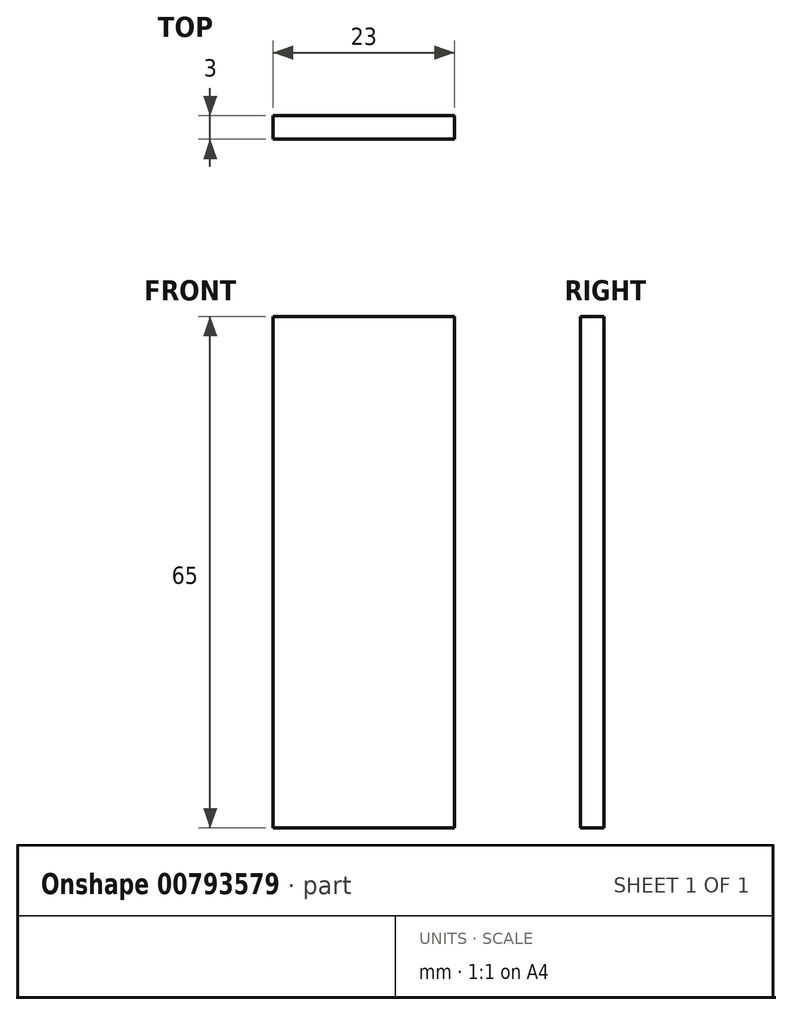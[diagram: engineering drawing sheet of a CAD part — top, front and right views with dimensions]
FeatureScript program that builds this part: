
annotation { "Feature Type Name" : "Feature", "Feature Type Description" : "" }
export const myFeature = defineFeature(function(context is Context, id is Id, definition is map)
    precondition{}
    {
        {
            var Q0;
            Q0=qCreatedBy(makeId("Front.planeOp"),FACE);
            var sketch = newSketch(context, id + "F0", { "sketchPlane" : qUnion([Q0])});
            skLineSegment(sketch, "E0.bottom", {"start": v(-60.68, 32.5) * mm, "end": v(49.32, 32.5) * mm});
            skLineSegment(sketch, "E0.top", {"start": v(-60.68, -32.5) * mm, "end": v(49.32, -32.5) * mm});
            skLineSegment(sketch, "E0.left", {"start": v(-60.68, 32.5) * mm, "end": v(-60.68, -32.5) * mm});
            skLineSegment(sketch, "E0.right", {"start": v(49.32, 32.5) * mm, "end": v(49.32, -32.5) * mm});
            skLineSegment(sketch, "E1.bottom", {"start": v(-14.35, 50) * mm, "end": v(8.65, 50) * mm});
            skLineSegment(sketch, "E1.top", {"start": v(-14.35, -50) * mm, "end": v(8.65, -50) * mm});
            skLineSegment(sketch, "E1.left", {"start": v(-14.35, 50) * mm, "end": v(-14.35, -50) * mm});
            skLineSegment(sketch, "E1.right", {"start": v(8.65, 50) * mm, "end": v(8.65, -50) * mm});
            skLineSegment(sketch, "E2", {"start": v(-14.35, 50) * mm, "end": v(-41, 32.5) * mm});
            skLineSegment(sketch, "E3", {"start": v(8.65, 50) * mm, "end": v(35.13, 32.5) * mm});
            skLineSegment(sketch, "E4", {"start": v(8.65, -50) * mm, "end": v(35.2, -32.5) * mm});
            skLineSegment(sketch, "E5", {"start": v(-14.35, -50) * mm, "end": v(-40.71, -32.5) * mm});
            skSolve(sketch);
        }
        {
            var Q0;
            Q0 = qSketchRegion(id + "F0", true);
            extrude(context, id + "F1", {"entities" : qUnion([Q0]), "depth" : 3 * mm, "offsetDistance" : 25 * mm});
        }
        {
            var Q0;
            Q0=makeQuery(id+"F1.opExtrude","CAP_FACE",FACE,{"disambiguationData":[OSD([sQuery(id+"F0.wireOp",EDGE,"E0.bottom"),sQuery(id+"F0.wireOp",EDGE,"E0.top"),sQuery(id+"F0.wireOp",EDGE,"E0.left"),sQuery(id+"F0.wireOp",EDGE,"E0.right"),sQuery(id+"F0.wireOp",EDGE,"E1.bottom"),sQuery(id+"F0.wireOp",EDGE,"E1.top"),sQuery(id+"F0.wireOp",EDGE,"E1.left"),sQuery(id+"F0.wireOp",EDGE,"E1.right"),sQuery(id+"F0.wireOp",EDGE,"E2"),sQuery(id+"F0.wireOp",EDGE,"E3"),sQuery(id+"F0.wireOp",EDGE,"E4"),sQuery(id+"F0.wireOp",EDGE,"E5")])],"isStart":false});
            var sketch = newSketch(context, id + "F2", { "sketchPlane" : qUnion([Q0])});
            skLineSegment(sketch, "E6.bottom", {"start": v(-14.35, 32.5) * mm, "end": v(8.65, 32.5) * mm});
            skLineSegment(sketch, "E6.top", {"start": v(-14.35, -32.5) * mm, "end": v(8.65, -32.5) * mm});
            skLineSegment(sketch, "E6.left", {"start": v(-14.35, 32.5) * mm, "end": v(-14.35, -32.5) * mm});
            skLineSegment(sketch, "E6.right", {"start": v(8.65, 32.5) * mm, "end": v(8.65, -32.5) * mm});
            skSolve(sketch);
        }
        {
            var Q0;
            Q0=makeQuery(id+"F2.imprint","IMPRINT",FACE,{"disambiguationData":[TD([[makeQuery(id+"F2.imprint","IMPRINT",EDGE,{"derivedFrom":sQuery(id+"F2.wireOp",EDGE,"E6.bottom")}),-1.0]])]});
            extrude(context, id + "F3", {"entities" : qUnion([Q0]), "depth" : 3 * mm, "offsetDistance" : 25 * mm});
        }
        {
            var Q0;
            Q0=makeQuery(id+"F1.opExtrude","CAP_FACE",FACE,{"disambiguationData":[OSD([sQuery(id+"F0.wireOp",EDGE,"E0.bottom"),sQuery(id+"F0.wireOp",EDGE,"E0.top"),sQuery(id+"F0.wireOp",EDGE,"E0.left"),sQuery(id+"F0.wireOp",EDGE,"E0.right"),sQuery(id+"F0.wireOp",EDGE,"E1.bottom"),sQuery(id+"F0.wireOp",EDGE,"E1.top"),sQuery(id+"F0.wireOp",EDGE,"E1.left"),sQuery(id+"F0.wireOp",EDGE,"E1.right"),sQuery(id+"F0.wireOp",EDGE,"E2"),sQuery(id+"F0.wireOp",EDGE,"E3"),sQuery(id+"F0.wireOp",EDGE,"E4"),sQuery(id+"F0.wireOp",EDGE,"E5")])],"isStart":false});
            var sketch = newSketch(context, id + "F4", { "sketchPlane" : qUnion([Q0])});
            skCircle(sketch, "E7", {"center": v(-15.85, 41.04) * mm, "radius": 1.5 * mm});
            skCircle(sketch, "E8", {"center": v(15.17, 41.61) * mm, "radius": 1.83 * mm});
            skSolve(sketch);
        }
        {
            var Q0;
            Q0=makeQuery(id+"F4.imprint","IMPRINT",FACE,{"disambiguationData":[TD([[makeQuery(id+"F4.imprint","IMPRINT",EDGE,{"derivedFrom":sQuery(id+"F4.wireOp",EDGE,"E8")}),1.0]])]});
            extrude(context, id + "F5", {"entities" : qUnion([Q0]), "operationType" : NewBodyOperationType.REMOVE, "oppositeDirection" : true, "depth" : 25 * mm, "offsetDistance" : 25 * mm});
        }
        {
            var Q0;
            Q0 = qSketchRegion(id + "F4", true);
            var Q1;
            Q1=makeQuery(id+"F1.opExtrude","CAP_FACE",FACE,{"disambiguationData":[OSD([sQuery(id+"F0.wireOp",EDGE,"E0.bottom"),sQuery(id+"F0.wireOp",EDGE,"E0.top"),sQuery(id+"F0.wireOp",EDGE,"E0.left"),sQuery(id+"F0.wireOp",EDGE,"E0.right"),sQuery(id+"F0.wireOp",EDGE,"E1.bottom"),sQuery(id+"F0.wireOp",EDGE,"E1.top"),sQuery(id+"F0.wireOp",EDGE,"E1.left"),sQuery(id+"F0.wireOp",EDGE,"E1.right"),sQuery(id+"F0.wireOp",EDGE,"E2"),sQuery(id+"F0.wireOp",EDGE,"E3"),sQuery(id+"F0.wireOp",EDGE,"E4"),sQuery(id+"F0.wireOp",EDGE,"E5")])],"isStart":false});
            extrude(context, id + "F6", {"entities" : qUnion([Q0, Q1]), "operationType" : NewBodyOperationType.REMOVE, "oppositeDirection" : true, "depth" : 25 * mm, "offsetDistance" : 25 * mm});
        }
        {
            var Q0;
            Q0 = qSketchRegion(id + "F4", true);
            extrude(context, id + "F7", {"entities" : qUnion([Q0]), "operationType" : NewBodyOperationType.REMOVE, "oppositeDirection" : true, "depth" : 25 * mm, "offsetDistance" : 25 * mm});
        }
    });
